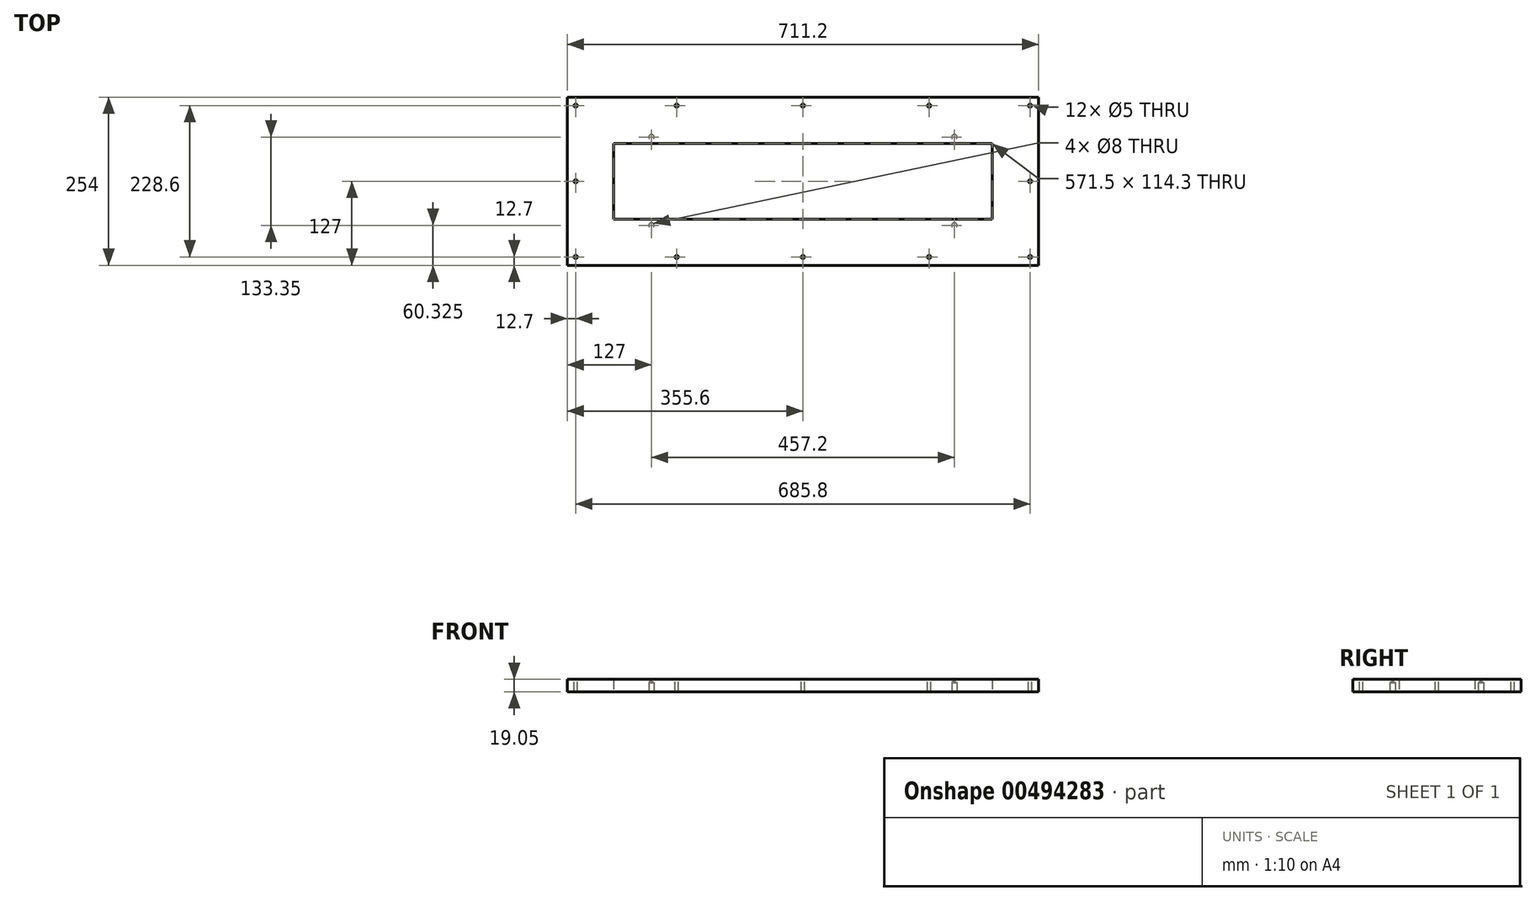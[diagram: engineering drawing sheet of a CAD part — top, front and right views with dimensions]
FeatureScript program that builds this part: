
annotation { "Feature Type Name" : "Feature", "Feature Type Description" : "" }
export const myFeature = defineFeature(function(context is Context, id is Id, definition is map)
    precondition{}
    {
        {
            var Q0;
            Q0=qCreatedBy(makeId("Top.planeOp"),FACE);
            var sketch = newSketch(context, id + "F0", { "sketchPlane" : qUnion([Q0])});
            skLineSegment(sketch, "E0.bottom", {"start": v(355.6, 127) * mm, "end": v(-355.6, 127) * mm});
            skLineSegment(sketch, "E0.top", {"start": v(355.6, -127) * mm, "end": v(-355.6, -127) * mm});
            skLineSegment(sketch, "E0.left", {"start": v(355.6, 127) * mm, "end": v(355.6, -127) * mm});
            skLineSegment(sketch, "E0.right", {"start": v(-355.6, 127) * mm, "end": v(-355.6, -127) * mm});
            skPoint(sketch, "E0.middle", {"position": v(0, 0) * mm});
            skLineSegment(sketch, "E1.bottom", {"start": v(285.75, 57.15) * mm, "end": v(-285.75, 57.15) * mm});
            skLineSegment(sketch, "E1.top", {"start": v(285.75, -57.15) * mm, "end": v(-285.75, -57.15) * mm});
            skLineSegment(sketch, "E1.left", {"start": v(285.75, 57.15) * mm, "end": v(285.75, -57.15) * mm});
            skLineSegment(sketch, "E1.right", {"start": v(-285.75, 57.15) * mm, "end": v(-285.75, -57.15) * mm});
            skSolve(sketch);
        }
        {
            var Q0;
            Q0=makeQuery(id+"F0.imprint","IMPRINT",FACE,{"disambiguationData":[TD([[makeQuery(id+"F0.imprint","IMPRINT",EDGE,{"derivedFrom":sQuery(id+"F0.wireOp",EDGE,"E0.bottom")}),1.0]])]});
            extrude(context, id + "F1", {"entities" : qUnion([Q0]), "depth" : 19.05 * mm});
        }
        {
            var Q0;
            Q0=makeQuery(id+"F1.opExtrude","CAP_FACE",FACE,{"disambiguationData":[OSD([sQuery(id+"F0.wireOp",EDGE,"E0.bottom"),sQuery(id+"F0.wireOp",EDGE,"E0.top"),sQuery(id+"F0.wireOp",EDGE,"E0.left"),sQuery(id+"F0.wireOp",EDGE,"E0.right"),sQuery(id+"F0.wireOp",EDGE,"E1.bottom"),sQuery(id+"F0.wireOp",EDGE,"E1.top"),sQuery(id+"F0.wireOp",EDGE,"E1.left"),sQuery(id+"F0.wireOp",EDGE,"E1.right")])],"isStart":false});
            var sketch = newSketch(context, id + "F2", { "sketchPlane" : qUnion([Q0])});
            skPoint(sketch, "E2.positionSnap0", {"position": v(0, 127) * mm});
            skLineSegment(sketch, "E3", {"start": v(-355.6, 127) * mm, "end": v(-355.6, 114.3) * mm});
            skLineSegment(sketch, "E4", {"start": v(-355.6, 114.3) * mm, "end": v(355.6, 114.3) * mm});
            skLineSegment(sketch, "E5", {"start": v(-355.6, 114.3) * mm, "end": v(-342.9, 114.3) * mm});
            skLineSegment(sketch, "E6", {"start": v(355.6, 114.3) * mm, "end": v(342.9, 114.3) * mm});
            skLineSegment(sketch, "E7", {"start": v(-342.9, 114.3) * mm, "end": v(-190.5, 114.3) * mm});
            skLineSegment(sketch, "E8", {"start": v(342.9, 114.3) * mm, "end": v(190.5, 114.3) * mm});
            skPoint(sketch, "E9", {"position": v(-342.9, 114.3) * mm});
            skPoint(sketch, "E10", {"position": v(-190.5, 114.3) * mm});
            skPoint(sketch, "E11", {"position": v(0, 114.3) * mm});
            skPoint(sketch, "E12", {"position": v(190.5, 114.3) * mm});
            skPoint(sketch, "E13", {"position": v(342.9, 114.3) * mm});
            skLineSegment(sketch, "E14", {"start": v(-355.6, -127) * mm, "end": v(-355.6, -114.3) * mm});
            skLineSegment(sketch, "E15", {"start": v(-355.6, -114.3) * mm, "end": v(355.6, -114.3) * mm});
            skLineSegment(sketch, "E16", {"start": v(355.6, -114.3) * mm, "end": v(342.9, -114.3) * mm});
            skLineSegment(sketch, "E17", {"start": v(342.9, -114.3) * mm, "end": v(190.5, -114.3) * mm});
            skLineSegment(sketch, "E18", {"start": v(-355.6, -114.3) * mm, "end": v(-342.9, -114.3) * mm});
            skLineSegment(sketch, "E19", {"start": v(-342.9, -114.3) * mm, "end": v(-190.5, -114.3) * mm});
            skLineSegment(sketch, "E20", {"start": v(-342.9, 114.3) * mm, "end": v(-342.9, 0) * mm});
            skLineSegment(sketch, "E21", {"start": v(342.9, 114.3) * mm, "end": v(342.9, 0) * mm});
            skPoint(sketch, "E22", {"position": v(-342.9, 0) * mm});
            skPoint(sketch, "E23", {"position": v(-342.9, -114.3) * mm});
            skPoint(sketch, "E24", {"position": v(-190.5, -114.3) * mm});
            skPoint(sketch, "E25", {"position": v(0, -114.3) * mm});
            skPoint(sketch, "E26", {"position": v(190.5, -114.3) * mm});
            skPoint(sketch, "E27", {"position": v(342.9, -114.3) * mm});
            skPoint(sketch, "E28", {"position": v(342.9, 0) * mm});
            skSolve(sketch);
        }
        {
            var Q0;
            Q0=sQuery(id+"F2.wireOp",VERTEX,"E9");
            var Q1;
            Q1=sQuery(id+"F2.wireOp",VERTEX,"E22");
            var Q2;
            Q2=sQuery(id+"F2.wireOp",VERTEX,"E10");
            var Q3;
            Q3=sQuery(id+"F2.wireOp",VERTEX,"E12");
            var Q4;
            Q4=sQuery(id+"F2.wireOp",VERTEX,"E13");
            var Q5;
            Q5=sQuery(id+"F2.wireOp",VERTEX,"E28");
            var Q6;
            Q6=sQuery(id+"F2.wireOp",VERTEX,"E27");
            var Q7;
            Q7=sQuery(id+"F2.wireOp",VERTEX,"E26");
            var Q8;
            Q8=sQuery(id+"F2.wireOp",VERTEX,"E24");
            var Q9;
            Q9=sQuery(id+"F2.wireOp",VERTEX,"E23");
            var Q10;
            Q10=sQuery(id+"F2.wireOp",VERTEX,"E11");
            var Q11;
            Q11=sQuery(id+"F2.wireOp",VERTEX,"E25");
            var Q12;
            Q12=makeQuery(id+"F1.opExtrude","SWEPT_BODY",BODY,{"disambiguationData":[OSD([sQuery(id+"F0.wireOp",EDGE,"E0.bottom"),sQuery(id+"F0.wireOp",EDGE,"E0.top"),sQuery(id+"F0.wireOp",EDGE,"E0.left"),sQuery(id+"F0.wireOp",EDGE,"E0.right"),sQuery(id+"F0.wireOp",EDGE,"E1.bottom"),sQuery(id+"F0.wireOp",EDGE,"E1.top"),sQuery(id+"F0.wireOp",EDGE,"E1.left"),sQuery(id+"F0.wireOp",EDGE,"E1.right")])]});
            hole(context, id + "F3", {"style" : HoleStyle.SIMPLE, "endStyle" : HoleEndStyle.BLIND, "holeDiameter" : 5 * mm, "holeDepth" : 19.05 * mm, "isTappedThrough" : true, "tappedDepth" : 12.7 * mm, "tapClearance" : 3, "startFromSketch" : true, "locations" : qUnion([Q0, Q1, Q2, Q3, Q4, Q5, Q6, Q7, Q8, Q9, Q10, Q11]), "scope" : qUnion([Q12])});
        }
        {
            var Q0;
            Q0=makeQuery(id+"F1.opExtrude","CAP_FACE",FACE,{"disambiguationData":[OSD([sQuery(id+"F0.wireOp",EDGE,"E0.bottom"),sQuery(id+"F0.wireOp",EDGE,"E0.top"),sQuery(id+"F0.wireOp",EDGE,"E0.left"),sQuery(id+"F0.wireOp",EDGE,"E0.right"),sQuery(id+"F0.wireOp",EDGE,"E1.bottom"),sQuery(id+"F0.wireOp",EDGE,"E1.top"),sQuery(id+"F0.wireOp",EDGE,"E1.left"),sQuery(id+"F0.wireOp",EDGE,"E1.right")])],"isStart":true});
            var sketch = newSketch(context, id + "F4", { "sketchPlane" : qUnion([Q0])});
            skLineSegment(sketch, "E29", {"start": v(-355.6, 127) * mm, "end": v(-355.6, 66.68) * mm});
            skLineSegment(sketch, "E30", {"start": v(-355.6, 66.68) * mm, "end": v(-228.6, 66.68) * mm});
            skLineSegment(sketch, "E31", {"start": v(-355.6, -127) * mm, "end": v(-355.6, -66.67) * mm});
            skLineSegment(sketch, "E32", {"start": v(-355.6, -66.67) * mm, "end": v(-228.6, -66.67) * mm});
            skLineSegment(sketch, "E33", {"start": v(355.6, 127) * mm, "end": v(228.6, 127) * mm});
            skLineSegment(sketch, "E34", {"start": v(228.6, 127) * mm, "end": v(228.6, 66.67) * mm});
            skLineSegment(sketch, "E35", {"start": v(355.6, -127) * mm, "end": v(355.6, -66.68) * mm});
            skLineSegment(sketch, "E36", {"start": v(355.6, -66.68) * mm, "end": v(228.6, -66.68) * mm});
            skPoint(sketch, "E37", {"position": v(-228.6, 66.68) * mm});
            skPoint(sketch, "E38", {"position": v(-228.6, -66.67) * mm});
            skPoint(sketch, "E39", {"position": v(228.6, 66.67) * mm});
            skPoint(sketch, "E40", {"position": v(228.6, -66.68) * mm});
            skSolve(sketch);
        }
        {
            var Q0;
            Q0=sQuery(id+"F4.wireOp",VERTEX,"E37");
            var Q1;
            Q1=sQuery(id+"F4.wireOp",VERTEX,"E38");
            var Q2;
            Q2=sQuery(id+"F4.wireOp",VERTEX,"E39");
            var Q3;
            Q3=sQuery(id+"F4.wireOp",VERTEX,"E40");
            var Q4;
            Q4=makeQuery(id+"F1.opExtrude","SWEPT_BODY",BODY,{"disambiguationData":[OSD([sQuery(id+"F0.wireOp",EDGE,"E0.bottom"),sQuery(id+"F0.wireOp",EDGE,"E0.top"),sQuery(id+"F0.wireOp",EDGE,"E0.left"),sQuery(id+"F0.wireOp",EDGE,"E0.right"),sQuery(id+"F0.wireOp",EDGE,"E1.bottom"),sQuery(id+"F0.wireOp",EDGE,"E1.top"),sQuery(id+"F0.wireOp",EDGE,"E1.left"),sQuery(id+"F0.wireOp",EDGE,"E1.right")])]});
            hole(context, id + "F5", {"style" : HoleStyle.SIMPLE, "endStyle" : HoleEndStyle.BLIND, "holeDiameter" : 8 * mm, "holeDepth" : 14.22 * mm, "isTappedThrough" : true, "tappedDepth" : 12.7 * mm, "tapClearance" : 3, "startFromSketch" : true, "locations" : qUnion([Q0, Q1, Q2, Q3]), "scope" : qUnion([Q4])});
        }
    });
